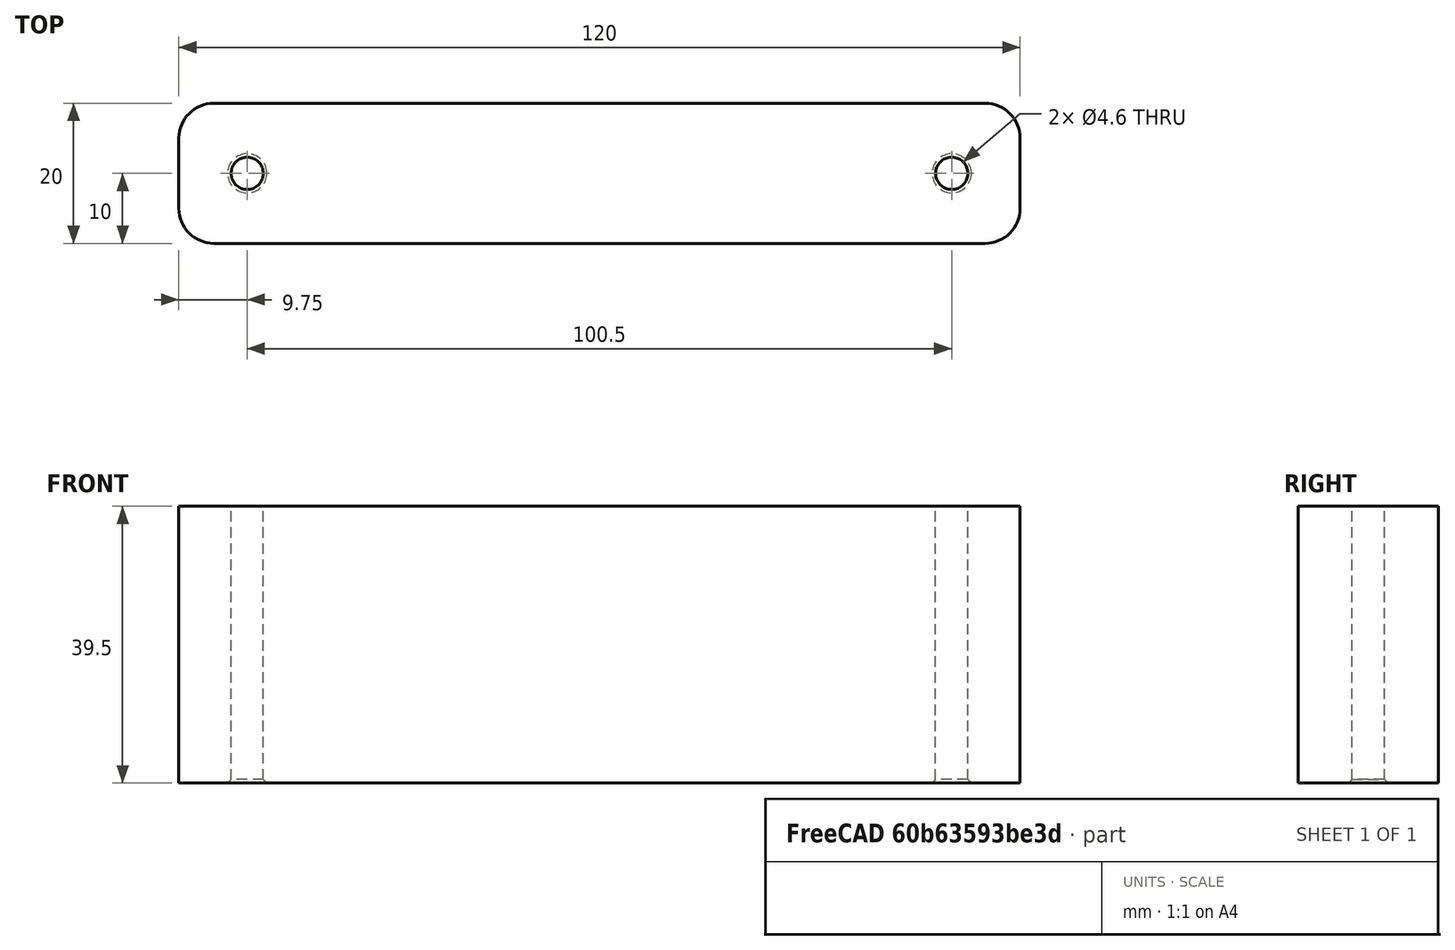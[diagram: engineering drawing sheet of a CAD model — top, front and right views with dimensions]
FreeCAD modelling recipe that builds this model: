
FCSTD DOCUMENT  (FreeCAD 0.17R13541 (Git))
Label: supports
License: All rights reserved
LicenseURL: http://en.wikipedia.org/wiki/All_rights_reserved
objects: Part::Cylinder×2, Part::Box×1, Part::MultiFuse×1, Part::Cut×1, Part::Fillet×1, Part::Chamfer×1
note: 7 computed .brp shape members not serialized (recipe doc carries the construction recipe); baked Part::Feature solids carry a one-line shape summary decoded from their .brp

FEATURE [Part::Box] Box  label="Cube"
  AttacherType = Attacher::AttachEngine3D
  Height = 39.5
  Length = 120
  Width = 20
FEATURE [Part::Cylinder] Cylinder
  Angle = 360
  AttacherType = Attacher::AttachEngine3D
  Height = 50
  Placement = pos=(9.75,10,-1) rot=(0,0,1;0rad)
  Radius = 2.3
FEATURE [Part::Cylinder] Cylinder001
  Angle = 360
  AttacherType = Attacher::AttachEngine3D
  Height = 50
  Placement = pos=(110.25,10,-1) rot=(0,0,1;0rad)
  Radius = 2.3
FEATURE [Part::MultiFuse] Fusion
  Shapes = -> [Cylinder001,Cylinder]
FEATURE [Part::Cut] Cut
  Base = -> Box
  Tool = -> Fusion
FEATURE [Part::Fillet] Fillet
  Base = -> Cut
  Edges = 4 edges r=5: [Edge1,Edge3,Edge6,Edge13]
FEATURE [Part::Chamfer] Chamfer
  Base = -> Fillet
  Edges = 2 edges r=0.5: [Edge23,Edge24]
